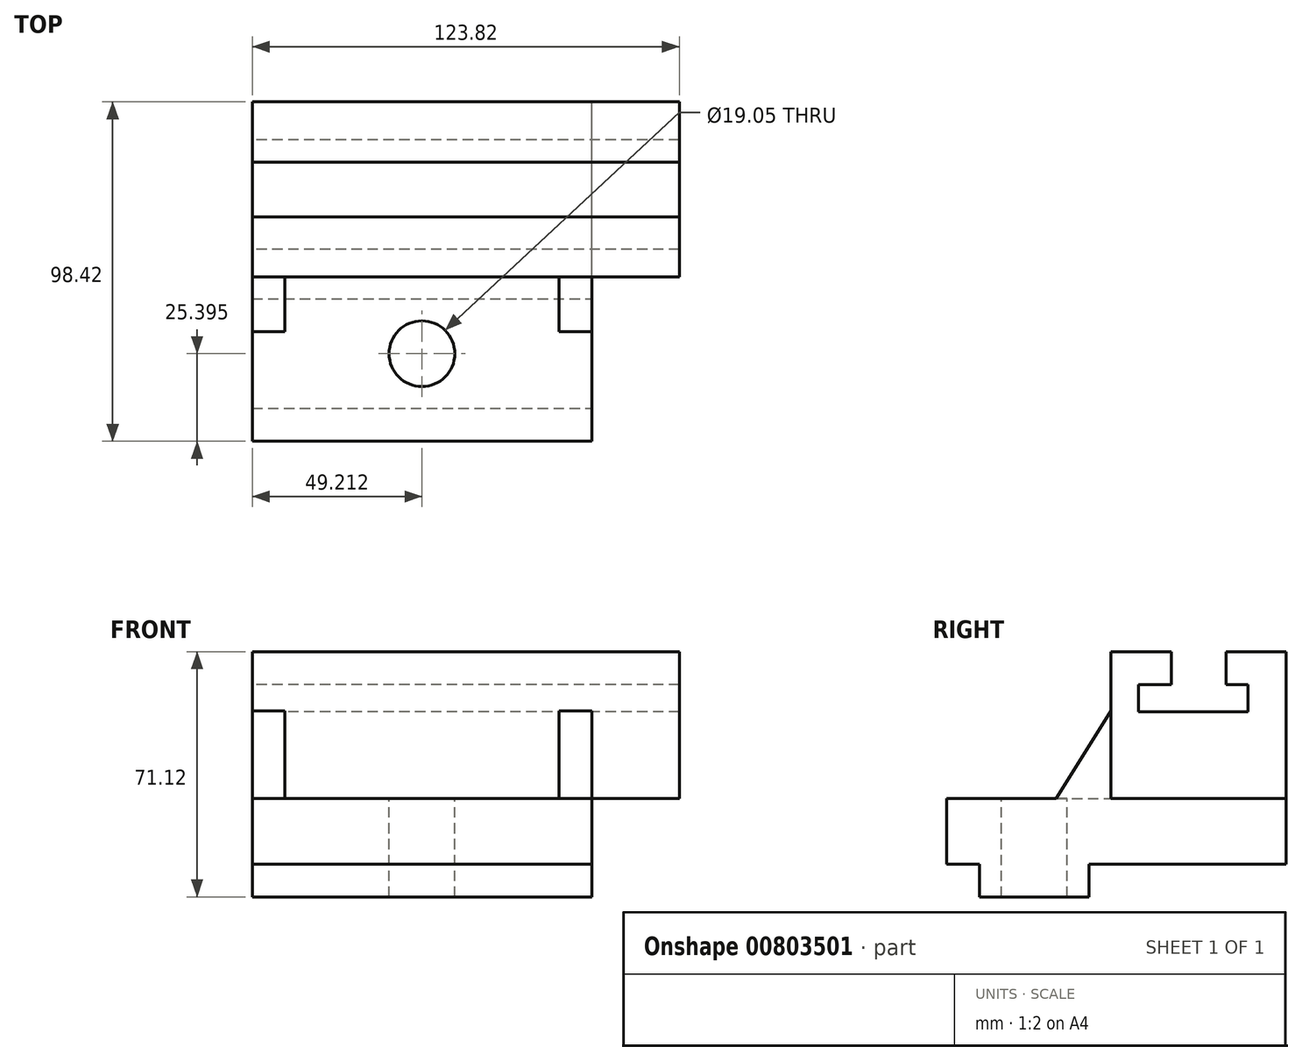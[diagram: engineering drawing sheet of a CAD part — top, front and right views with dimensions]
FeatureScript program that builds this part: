
annotation { "Feature Type Name" : "Feature", "Feature Type Description" : "" }
export const myFeature = defineFeature(function(context is Context, id is Id, definition is map)
    precondition{}
    {
        {
            var Q0;
            Q0=qCreatedBy(makeId("Front.planeOp"),FACE);
            var sketch = newSketch(context, id + "F0", { "sketchPlane" : qUnion([Q0])});
            skLineSegment(sketch, "E0.bottom", {"start": v(-91.95, 29.53) * mm, "end": v(6.47, 29.53) * mm});
            skLineSegment(sketch, "E0.top", {"start": v(-91.95, 10.48) * mm, "end": v(6.47, 10.48) * mm});
            skLineSegment(sketch, "E0.left", {"start": v(-91.95, 29.53) * mm, "end": v(-91.95, 10.48) * mm});
            skLineSegment(sketch, "E0.right", {"start": v(6.47, 29.53) * mm, "end": v(6.47, 10.48) * mm});
            skSolve(sketch);
        }
        {
            var Q0;
            Q0 = qSketchRegion(id + "F0", true);
            extrude(context, id + "F1", {"entities" : qUnion([Q0]), "depth" : 98.42 * mm, "offsetDistance" : 25.4 * mm});
        }
        {
            var Q0;
            Q0=makeQuery(id+"F1.opExtrude","SWEPT_FACE",FACE,{"disambiguationData":[OSD([sQuery(id+"F0.wireOp",EDGE,"E0.bottom")])]});
            var sketch = newSketch(context, id + "F2", { "sketchPlane" : qUnion([Q0])});
            skLineSegment(sketch, "E1.bottom", {"start": v(-91.95, 0) * mm, "end": v(31.87, 0) * mm});
            skLineSegment(sketch, "E1.top", {"start": v(-91.95, -50.8) * mm, "end": v(31.87, -50.8) * mm});
            skLineSegment(sketch, "E1.left", {"start": v(-91.95, 0) * mm, "end": v(-91.95, -50.8) * mm});
            skLineSegment(sketch, "E1.right", {"start": v(31.87, 0) * mm, "end": v(31.87, -50.8) * mm});
            skSolve(sketch);
        }
        {
            var Q0;
            Q0 = qSketchRegion(id + "F2", true);
            extrude(context, id + "F3", {"entities" : qUnion([Q0]), "operationType" : NewBodyOperationType.ADD, "depth" : 42.55 * mm, "offsetDistance" : 25.4 * mm});
        }
        {
            var Q0;
            Q0=makeQuery(id+"F3.boolean.opBoolean","MERGE",FACE,{"derivedFrom":[makeQuery(id+"F1.opExtrude","SWEPT_FACE",FACE,{"disambiguationData":[OSD([sQuery(id+"F0.wireOp",EDGE,"E0.left")])]}),makeQuery(id+"F3.opExtrude","SWEPT_FACE",FACE,{"disambiguationData":[OSD([sQuery(id+"F2.wireOp",EDGE,"E1.left")])]})]});
            var sketch = newSketch(context, id + "F4", { "sketchPlane" : qUnion([Q0])});
            skLineSegment(sketch, "E2", {"start": v(17.46, 72.07) * mm, "end": v(17.46, 62.55) * mm});
            skLineSegment(sketch, "E3", {"start": v(17.46, 62.55) * mm, "end": v(11.07, 62.55) * mm});
            skLineSegment(sketch, "E4", {"start": v(11.07, 62.55) * mm, "end": v(11.07, 54.61) * mm});
            skLineSegment(sketch, "E5", {"start": v(11.07, 54.61) * mm, "end": v(42.82, 54.61) * mm});
            skLineSegment(sketch, "E6", {"start": v(42.82, 54.61) * mm, "end": v(42.82, 62.55) * mm});
            skLineSegment(sketch, "E7", {"start": v(42.82, 62.55) * mm, "end": v(33.34, 62.55) * mm});
            skLineSegment(sketch, "E8", {"start": v(33.34, 62.55) * mm, "end": v(33.34, 72.07) * mm});
            skLineSegment(sketch, "E9", {"start": v(33.34, 72.07) * mm, "end": v(17.46, 72.07) * mm});
            skSolve(sketch);
        }
        {
            var Q0;
            Q0=makeQuery(id+"F3.opExtrude","SWEPT_FACE",FACE,{"disambiguationData":[OSD([sQuery(id+"F2.wireOp",EDGE,"E1.top")])]});
            var sketch = newSketch(context, id + "F5", { "sketchPlane" : qUnion([Q0])});
            skLineSegment(sketch, "E10.bottom", {"start": v(-91.95, 54.93) * mm, "end": v(-82.43, 54.93) * mm});
            skLineSegment(sketch, "E10.top", {"start": v(-91.95, 29.53) * mm, "end": v(-82.43, 29.53) * mm});
            skLineSegment(sketch, "E10.left", {"start": v(-91.95, 54.93) * mm, "end": v(-91.95, 29.53) * mm});
            skLineSegment(sketch, "E10.right", {"start": v(-82.43, 54.93) * mm, "end": v(-82.43, 29.53) * mm});
            skSolve(sketch);
        }
        {
            var Q0;
            Q0 = qSketchRegion(id + "F5", true);
            extrude(context, id + "F6", {"entities" : qUnion([Q0]), "operationType" : NewBodyOperationType.ADD, "depth" : 15.88 * mm, "offsetDistance" : 25.4 * mm});
        }
        {
            var Q0;
            Q0=makeQuery(id+"F6.boolean.opBoolean","MERGE",FACE,{"derivedFrom":[makeQuery(id+"F3.boolean.opBoolean","MERGE",FACE,{"derivedFrom":[makeQuery(id+"F1.opExtrude","SWEPT_FACE",FACE,{"disambiguationData":[OSD([sQuery(id+"F0.wireOp",EDGE,"E0.left")])]}),makeQuery(id+"F3.opExtrude","SWEPT_FACE",FACE,{"disambiguationData":[OSD([sQuery(id+"F2.wireOp",EDGE,"E1.left")])]})]}),makeQuery(id+"F6.opExtrude","SWEPT_FACE",FACE,{"disambiguationData":[OSD([sQuery(id+"F5.wireOp",EDGE,"E10.left")])]})]});
            var sketch = newSketch(context, id + "F7", { "sketchPlane" : qUnion([Q0])});
            skLineSegment(sketch, "E11", {"start": v(50.8, 54.93) * mm, "end": v(66.67, 29.53) * mm});
            skLineSegment(sketch, "E12", {"start": v(50.8, 54.93) * mm, "end": v(66.67, 54.93) * mm});
            skLineSegment(sketch, "E13", {"start": v(66.67, 54.93) * mm, "end": v(66.67, 29.53) * mm});
            skSolve(sketch);
        }
        {
            var Q0;
            Q0 = qSketchRegion(id + "F7", true);
            extrude(context, id + "F8", {"entities" : qUnion([Q0]), "operationType" : NewBodyOperationType.REMOVE, "endBound" : BoundingType.THROUGH_ALL, "oppositeDirection" : true, "depth" : 25.4 * mm, "offsetDistance" : 25.4 * mm});
        }
        {
            var Q0;
            Q0=makeQuery(id+"F3.opExtrude","SWEPT_FACE",FACE,{"disambiguationData":[OSD([sQuery(id+"F2.wireOp",EDGE,"E1.top")])]});
            var sketch = newSketch(context, id + "F9", { "sketchPlane" : qUnion([Q0])});
            skLineSegment(sketch, "E14.bottom", {"start": v(6.47, 29.53) * mm, "end": v(-3.05, 29.53) * mm});
            skLineSegment(sketch, "E14.top", {"start": v(6.47, 54.93) * mm, "end": v(-3.05, 54.93) * mm});
            skLineSegment(sketch, "E14.left", {"start": v(6.47, 29.53) * mm, "end": v(6.47, 54.93) * mm});
            skLineSegment(sketch, "E14.right", {"start": v(-3.05, 29.53) * mm, "end": v(-3.05, 54.93) * mm});
            skSolve(sketch);
        }
        {
            var Q0;
            Q0 = qSketchRegion(id + "F9", true);
            extrude(context, id + "F10", {"entities" : qUnion([Q0]), "operationType" : NewBodyOperationType.ADD, "depth" : 15.88 * mm, "offsetDistance" : 25.4 * mm});
        }
        {
            var Q0;
            Q0=makeQuery(id+"F10.boolean.opBoolean","MERGE",FACE,{"derivedFrom":[makeQuery(id+"F1.opExtrude","SWEPT_FACE",FACE,{"disambiguationData":[OSD([sQuery(id+"F0.wireOp",EDGE,"E0.right")])]}),makeQuery(id+"F10.opExtrude","SWEPT_FACE",FACE,{"disambiguationData":[OSD([sQuery(id+"F9.wireOp",EDGE,"E14.left")])]})]});
            var sketch = newSketch(context, id + "F11", { "sketchPlane" : qUnion([Q0])});
            skLineSegment(sketch, "E15", {"start": v(-50.8, 54.93) * mm, "end": v(-66.67, 29.53) * mm});
            skLineSegment(sketch, "E16", {"start": v(-66.67, 54.93) * mm, "end": v(-66.67, 29.53) * mm});
            skLineSegment(sketch, "E17", {"start": v(-66.67, 54.93) * mm, "end": v(-50.8, 54.93) * mm});
            skSolve(sketch);
        }
        {
            var Q0;
            Q0 = qSketchRegion(id + "F11", true);
            extrude(context, id + "F12", {"entities" : qUnion([Q0]), "operationType" : NewBodyOperationType.REMOVE, "endBound" : BoundingType.THROUGH_ALL, "oppositeDirection" : true, "depth" : 25.4 * mm, "offsetDistance" : 25.4 * mm});
        }
        {
            var Q0;
            Q0=makeQuery(id+"F10.boolean.opBoolean","MERGE",FACE,{"derivedFrom":[makeQuery(id+"F1.opExtrude","SWEPT_FACE",FACE,{"disambiguationData":[OSD([sQuery(id+"F0.wireOp",EDGE,"E0.right")])]}),makeQuery(id+"F10.opExtrude","SWEPT_FACE",FACE,{"disambiguationData":[OSD([sQuery(id+"F9.wireOp",EDGE,"E14.left")])]})]});
            var sketch = newSketch(context, id + "F13", { "sketchPlane" : qUnion([Q0])});
            skLineSegment(sketch, "E18.bottom", {"start": v(-88.9, 10.48) * mm, "end": v(-57.15, 10.48) * mm});
            skLineSegment(sketch, "E18.top", {"start": v(-88.9, 0.95) * mm, "end": v(-57.15, 0.95) * mm});
            skLineSegment(sketch, "E18.left", {"start": v(-88.9, 10.48) * mm, "end": v(-88.9, 0.95) * mm});
            skLineSegment(sketch, "E18.right", {"start": v(-57.15, 10.48) * mm, "end": v(-57.15, 0.95) * mm});
            skSolve(sketch);
        }
        {
            var Q0;
            Q0 = qSketchRegion(id + "F13", true);
            extrude(context, id + "F14", {"entities" : qUnion([Q0]), "operationType" : NewBodyOperationType.ADD, "oppositeDirection" : true, "depth" : 98.42 * mm, "offsetDistance" : 25.4 * mm});
        }
        {
            var Q0;
            Q0 = qSketchRegion(id + "F4", true);
            extrude(context, id + "F15", {"entities" : qUnion([Q0]), "operationType" : NewBodyOperationType.REMOVE, "endBound" : BoundingType.THROUGH_ALL, "oppositeDirection" : true, "depth" : 25.4 * mm, "offsetDistance" : 25.4 * mm});
        }
        {
            var Q0;
            Q0=makeQuery(id+"F1.opExtrude","SWEPT_FACE",FACE,{"disambiguationData":[OSD([sQuery(id+"F0.wireOp",EDGE,"E0.bottom")])]});
            var sketch = newSketch(context, id + "F16", { "sketchPlane" : qUnion([Q0])});
            skCircle(sketch, "E19", {"center": v(-42.74, -73.03) * mm, "radius": 9.53 * mm});
            skSolve(sketch);
        }
        {
            var Q0;
            Q0 = qSketchRegion(id + "F16", true);
            extrude(context, id + "F17", {"entities" : qUnion([Q0]), "operationType" : NewBodyOperationType.REMOVE, "endBound" : BoundingType.THROUGH_ALL, "oppositeDirection" : true, "depth" : 25.4 * mm, "offsetDistance" : 25.4 * mm});
        }
    });
